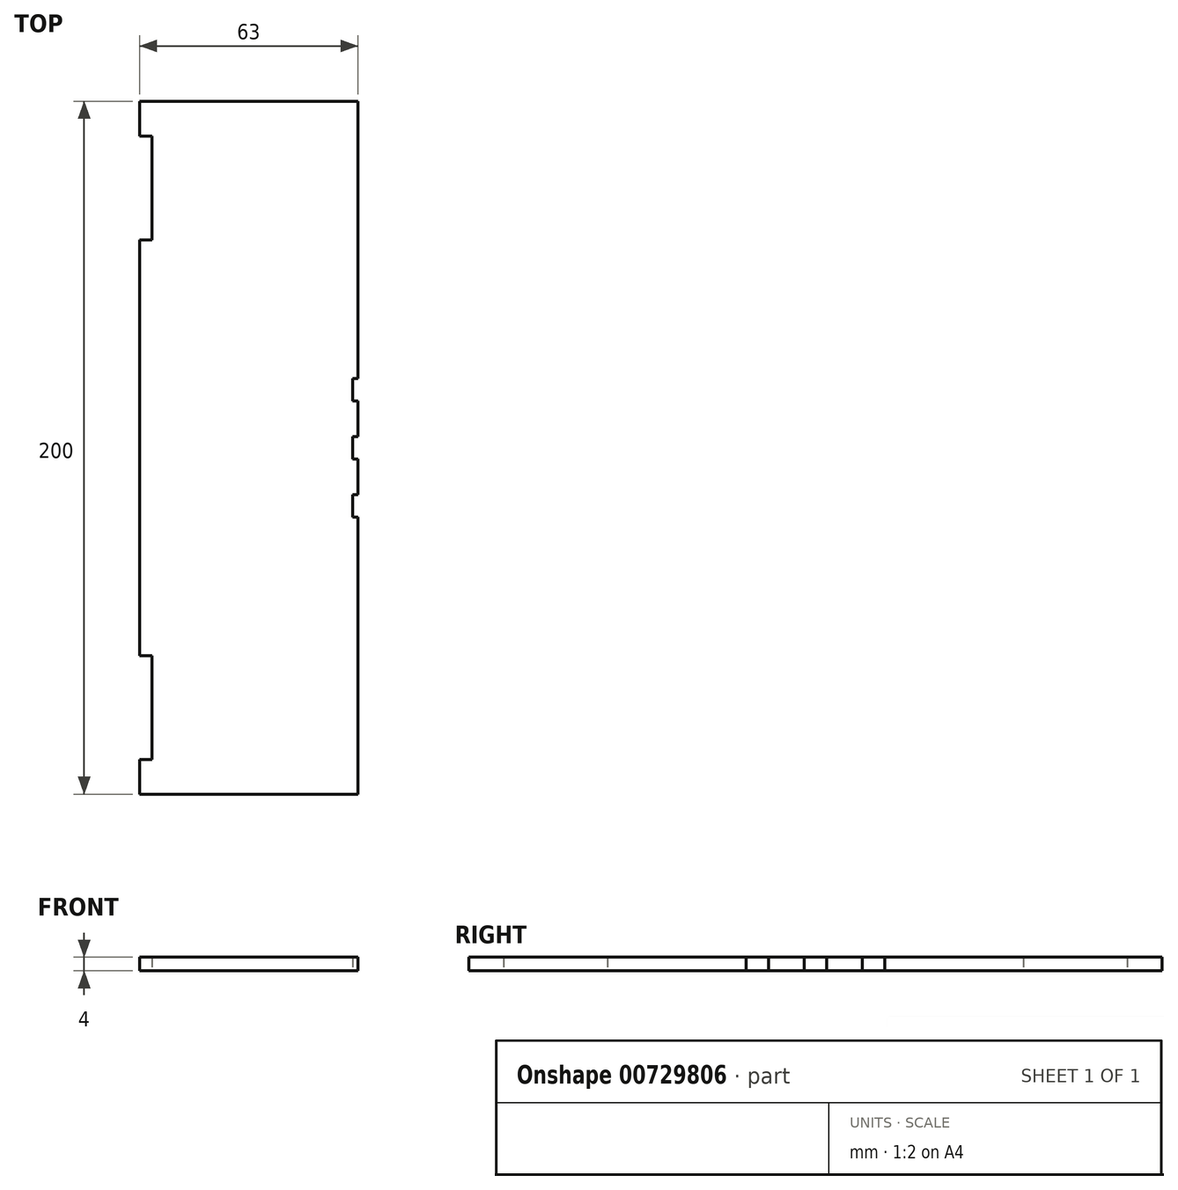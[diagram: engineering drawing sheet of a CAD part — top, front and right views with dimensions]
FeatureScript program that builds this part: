
annotation { "Feature Type Name" : "Feature", "Feature Type Description" : "" }
export const myFeature = defineFeature(function(context is Context, id is Id, definition is map)
    precondition{}
    {
        {
            var Q0;
            Q0=qCreatedBy(makeId("Top.planeOp"),FACE);
            var sketch = newSketch(context, id + "F0", { "sketchPlane" : qUnion([Q0])});
            skLineSegment(sketch, "E0", {"start": v(0, 0) * mm, "end": v(0, 200) * mm, "construction": true});
            skLineSegment(sketch, "E1", {"start": v(0, 200) * mm, "end": v(-5, 200) * mm, "construction": true});
            skLineSegment(sketch, "E2", {"start": v(-5, 200) * mm, "end": v(-68, 200) * mm});
            skLineSegment(sketch, "E3", {"start": v(-68, 200) * mm, "end": v(-68, 190) * mm});
            skLineSegment(sketch, "E4", {"start": v(-68, 0) * mm, "end": v(-5, 0) * mm});
            skLineSegment(sketch, "E5", {"start": v(-5, 0) * mm, "end": v(0, 0) * mm, "construction": true});
            skLineSegment(sketch, "E6", {"start": v(-5, 0) * mm, "end": v(-5, 80) * mm});
            skLineSegment(sketch, "E7", {"start": v(-5, 80) * mm, "end": v(-6.5, 80) * mm});
            skLineSegment(sketch, "E8", {"start": v(-6.5, 80) * mm, "end": v(-6.5, 86.5) * mm});
            skLineSegment(sketch, "E9", {"start": v(-6.5, 86.5) * mm, "end": v(-5, 86.5) * mm});
            skLineSegment(sketch, "E10", {"start": v(-5, 86.5) * mm, "end": v(-5, 96.75) * mm});
            skLineSegment(sketch, "E11", {"start": v(-5, 96.75) * mm, "end": v(-6.5, 96.75) * mm});
            skLineSegment(sketch, "E12", {"start": v(-6.5, 96.75) * mm, "end": v(-6.5, 103.25) * mm});
            skLineSegment(sketch, "E13", {"start": v(-6.5, 103.25) * mm, "end": v(-5, 103.25) * mm});
            skLineSegment(sketch, "E14", {"start": v(-5, 103.25) * mm, "end": v(-5, 113.5) * mm});
            skLineSegment(sketch, "E15", {"start": v(-5, 113.5) * mm, "end": v(-6.5, 113.5) * mm});
            skLineSegment(sketch, "E16", {"start": v(-6.5, 113.5) * mm, "end": v(-6.5, 120) * mm});
            skLineSegment(sketch, "E17", {"start": v(-6.5, 120) * mm, "end": v(-5, 120) * mm});
            skLineSegment(sketch, "E18", {"start": v(-5, 120) * mm, "end": v(-5, 200) * mm});
            skLineSegment(sketch, "E19", {"start": v(-68, 10) * mm, "end": v(-64.5, 10) * mm});
            skLineSegment(sketch, "E20", {"start": v(-64.5, 10) * mm, "end": v(-64.5, 40) * mm});
            skLineSegment(sketch, "E21", {"start": v(-64.5, 40) * mm, "end": v(-68, 40) * mm});
            skLineSegment(sketch, "E22", {"start": v(-68, 160) * mm, "end": v(-64.5, 160) * mm});
            skLineSegment(sketch, "E23", {"start": v(-64.5, 160) * mm, "end": v(-64.5, 190) * mm});
            skLineSegment(sketch, "E24", {"start": v(-64.5, 190) * mm, "end": v(-68, 190) * mm});
            skLineSegment(sketch, "E25.trimOffspring", {"start": v(-68, 160) * mm, "end": v(-68, 40) * mm});
            skLineSegment(sketch, "E26.trimOffspring", {"start": v(-68, 10) * mm, "end": v(-68, 0) * mm});
            skSolve(sketch);
        }
        {
            var Q0;
            Q0 = qSketchRegion(id + "F0", true);
            extrude(context, id + "F1", {"entities" : qUnion([Q0]), "depth" : 4 * mm, "offsetDistance" : 25 * mm});
        }
    });
